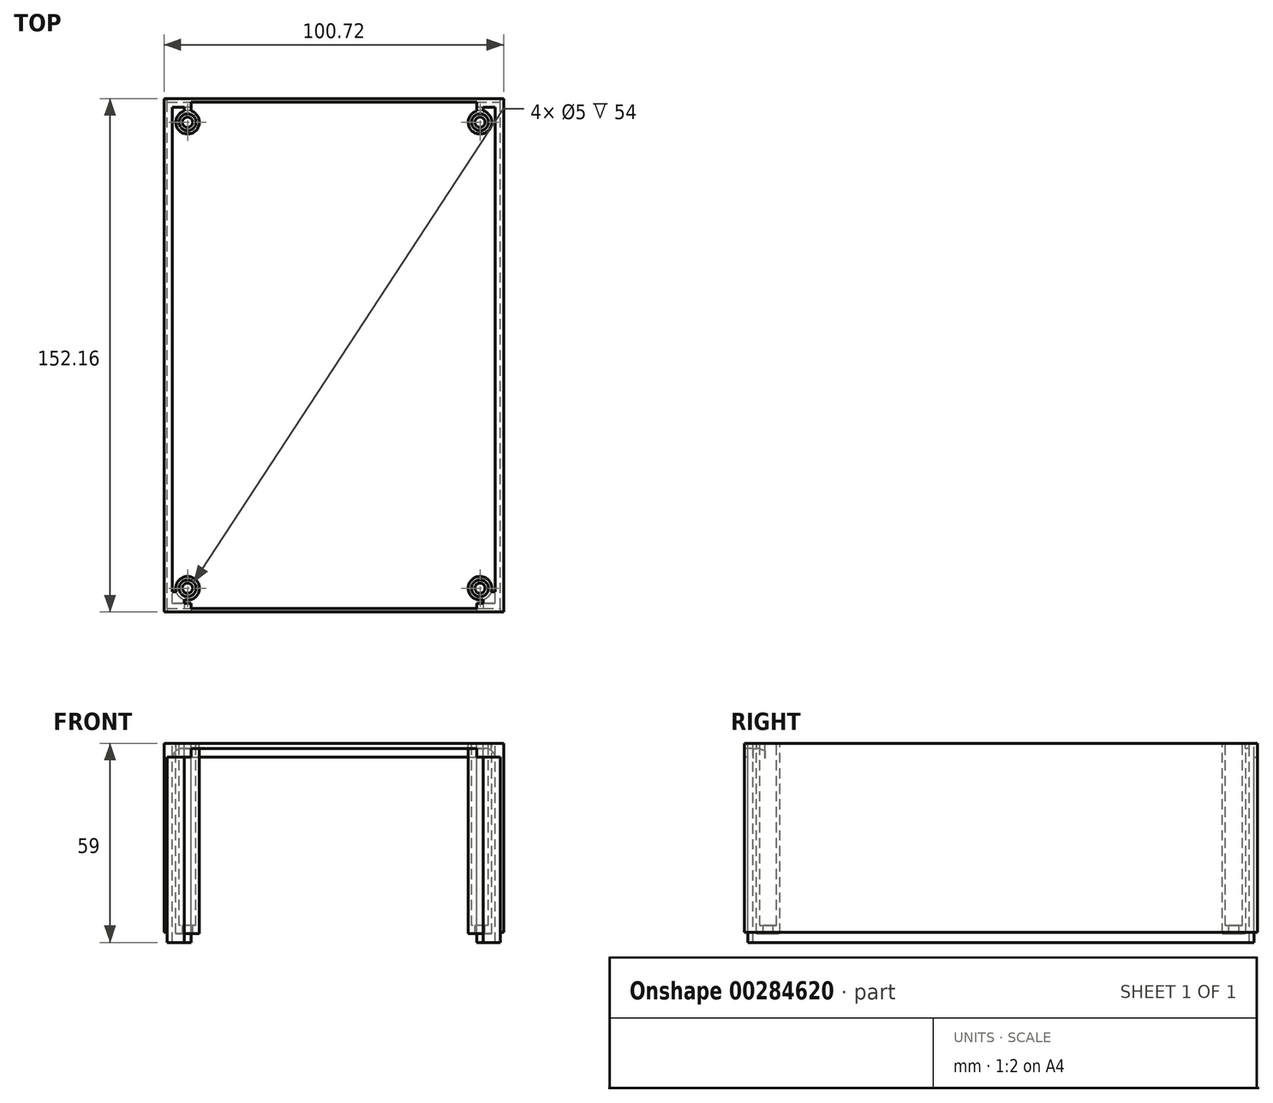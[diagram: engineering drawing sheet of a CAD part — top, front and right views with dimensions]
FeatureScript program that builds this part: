
annotation { "Feature Type Name" : "Feature", "Feature Type Description" : "" }
export const myFeature = defineFeature(function(context is Context, id is Id, definition is map)
    precondition{}
    {
        {
            var Q0;
            Q0=qCreatedBy(makeId("Top.planeOp"),FACE);
            var sketch = newSketch(context, id + "F0", { "sketchPlane" : qUnion([Q0])});
            skLineSegment(sketch, "E0.bottom", {"start": v(50.36, -76.08) * mm, "end": v(-50.36, -76.08) * mm});
            skLineSegment(sketch, "E0.top", {"start": v(50.36, 76.07) * mm, "end": v(-50.36, 76.07) * mm});
            skLineSegment(sketch, "E0.left", {"start": v(50.36, -76.08) * mm, "end": v(50.36, 76.08) * mm});
            skLineSegment(sketch, "E0.right", {"start": v(-50.36, -76.08) * mm, "end": v(-50.36, 76.07) * mm});
            skLineSegment(sketch, "E1.bottom", {"start": v(47.86, -73.58) * mm, "end": v(-47.86, -73.58) * mm});
            skLineSegment(sketch, "E1.top", {"start": v(47.86, 73.58) * mm, "end": v(-47.86, 73.58) * mm});
            skLineSegment(sketch, "E1.left", {"start": v(47.86, -73.58) * mm, "end": v(47.86, 73.58) * mm});
            skLineSegment(sketch, "E1.right", {"start": v(-47.86, -73.58) * mm, "end": v(-47.86, 73.58) * mm});
            skLineSegment(sketch, "E2.bottom", {"start": v(-49.36, -75.08) * mm, "end": v(49.36, -75.08) * mm});
            skLineSegment(sketch, "E2.top", {"start": v(-49.36, 75.08) * mm, "end": v(49.36, 75.08) * mm});
            skLineSegment(sketch, "E2.left", {"start": v(-49.36, -75.08) * mm, "end": v(-49.36, 75.08) * mm});
            skLineSegment(sketch, "E2.right", {"start": v(49.36, -75.08) * mm, "end": v(49.36, 75.08) * mm});
            skPoint(sketch, "E3", {"position": v(0, -76.08) * mm});
            skLineSegment(sketch, "E4", {"start": v(10.09, -76.08) * mm, "end": v(-10.09, -76.08) * mm});
            skLineSegment(sketch, "E5", {"start": v(-10.09, -73.58) * mm, "end": v(10.09, -73.58) * mm});
            skCircle(sketch, "E6", {"center": v(43.36, -69.08) * mm, "radius": 3.5 * mm});
            skCircle(sketch, "E7", {"center": v(43.36, -69.08) * mm, "radius": 2.5 * mm});
            skCircle(sketch, "E8", {"center": v(43.36, -69.08) * mm, "radius": 1.5 * mm});
            skCircle(sketch, "E9", {"center": v(43.36, 69.08) * mm, "radius": 1.5 * mm});
            skCircle(sketch, "E10", {"center": v(43.36, 69.08) * mm, "radius": 2.5 * mm});
            skCircle(sketch, "E11", {"center": v(43.36, 69.08) * mm, "radius": 3.5 * mm});
            skCircle(sketch, "E12", {"center": v(-43.36, 69.08) * mm, "radius": 1.5 * mm});
            skCircle(sketch, "E13", {"center": v(-43.36, 69.08) * mm, "radius": 2.5 * mm});
            skCircle(sketch, "E14", {"center": v(-43.36, 69.08) * mm, "radius": 3.5 * mm});
            skCircle(sketch, "E15", {"center": v(-43.36, -69.08) * mm, "radius": 1.5 * mm});
            skCircle(sketch, "E16", {"center": v(-43.36, -69.08) * mm, "radius": 2.5 * mm});
            skCircle(sketch, "E17", {"center": v(-43.36, -69.08) * mm, "radius": 3.5 * mm});
            skLineSegment(sketch, "E18", {"start": v(49.36, -75.08) * mm, "end": v(49.36, -76.08) * mm});
            skLineSegment(sketch, "E19", {"start": v(-49.36, -75.08) * mm, "end": v(-49.36, -76.08) * mm});
            skLineSegment(sketch, "E20", {"start": v(-49.36, 75.08) * mm, "end": v(-49.36, 76.07) * mm});
            skLineSegment(sketch, "E21", {"start": v(49.36, 75.08) * mm, "end": v(49.36, 76.07) * mm});
            skLineSegment(sketch, "E22", {"start": v(-47.86, -73.58) * mm, "end": v(-49.36, -73.58) * mm});
            skLineSegment(sketch, "E23", {"start": v(47.86, -73.58) * mm, "end": v(49.36, -73.58) * mm});
            skLineSegment(sketch, "E24", {"start": v(47.86, 73.58) * mm, "end": v(49.36, 73.58) * mm});
            skLineSegment(sketch, "E25", {"start": v(-47.86, 73.58) * mm, "end": v(-49.36, 73.58) * mm});
            skLineSegment(sketch, "E26.bottom", {"start": v(47.86, 68.08) * mm, "end": v(45.65, 68.08) * mm});
            skLineSegment(sketch, "E26.top", {"start": v(47.86, 70.08) * mm, "end": v(45.65, 70.08) * mm});
            skLineSegment(sketch, "E26.left", {"start": v(47.86, 68.08) * mm, "end": v(47.86, 70.08) * mm});
            skLineSegment(sketch, "E27.bottom", {"start": v(42.36, 73.58) * mm, "end": v(44.36, 73.58) * mm});
            skLineSegment(sketch, "E27.left", {"start": v(42.36, 73.58) * mm, "end": v(42.36, 71.37) * mm});
            skLineSegment(sketch, "E27.right", {"start": v(44.36, 73.58) * mm, "end": v(44.36, 71.37) * mm});
            skLineSegment(sketch, "E28.bottom", {"start": v(-44.36, 73.58) * mm, "end": v(-42.36, 73.58) * mm});
            skLineSegment(sketch, "E28.left", {"start": v(-44.36, 73.58) * mm, "end": v(-44.36, 71.37) * mm});
            skLineSegment(sketch, "E28.right", {"start": v(-42.36, 73.58) * mm, "end": v(-42.36, 71.37) * mm});
            skLineSegment(sketch, "E29.bottom", {"start": v(-47.86, 70.08) * mm, "end": v(-45.65, 70.08) * mm});
            skLineSegment(sketch, "E29.top", {"start": v(-47.86, 68.08) * mm, "end": v(-45.65, 68.08) * mm});
            skLineSegment(sketch, "E29.left", {"start": v(-47.86, 70.08) * mm, "end": v(-47.86, 68.08) * mm});
            skLineSegment(sketch, "E30.bottom", {"start": v(-47.86, -68.08) * mm, "end": v(-45.65, -68.08) * mm});
            skLineSegment(sketch, "E30.top", {"start": v(-47.86, -70.08) * mm, "end": v(-45.65, -70.08) * mm});
            skLineSegment(sketch, "E30.left", {"start": v(-47.86, -68.08) * mm, "end": v(-47.86, -70.08) * mm});
            skLineSegment(sketch, "E31.bottom", {"start": v(-42.36, -73.58) * mm, "end": v(-44.36, -73.58) * mm});
            skLineSegment(sketch, "E31.left", {"start": v(-42.36, -73.58) * mm, "end": v(-42.36, -71.37) * mm});
            skLineSegment(sketch, "E31.right", {"start": v(-44.36, -73.58) * mm, "end": v(-44.36, -71.37) * mm});
            skLineSegment(sketch, "E32.bottom", {"start": v(44.36, -73.58) * mm, "end": v(42.36, -73.58) * mm});
            skLineSegment(sketch, "E32.left", {"start": v(44.36, -73.58) * mm, "end": v(44.36, -71.37) * mm});
            skLineSegment(sketch, "E32.right", {"start": v(42.36, -73.58) * mm, "end": v(42.36, -71.37) * mm});
            skLineSegment(sketch, "E33.bottom", {"start": v(47.86, -70.08) * mm, "end": v(45.65, -70.08) * mm});
            skLineSegment(sketch, "E33.top", {"start": v(47.86, -68.08) * mm, "end": v(45.65, -68.08) * mm});
            skLineSegment(sketch, "E33.left", {"start": v(47.86, -70.08) * mm, "end": v(47.86, -68.08) * mm});
            skLineSegment(sketch, "E34", {"start": v(-42.36, 73.58) * mm, "end": v(-42.36, 76.07) * mm});
            skLineSegment(sketch, "E35", {"start": v(42.36, 73.58) * mm, "end": v(42.36, 76.07) * mm});
            skLineSegment(sketch, "E36", {"start": v(42.36, -73.58) * mm, "end": v(42.36, -76.08) * mm});
            skLineSegment(sketch, "E37", {"start": v(44.36, -73.58) * mm, "end": v(44.36, -76.08) * mm});
            skLineSegment(sketch, "E38", {"start": v(-44.36, -73.58) * mm, "end": v(-44.36, -76.08) * mm});
            skLineSegment(sketch, "E39", {"start": v(-42.36, -73.58) * mm, "end": v(-42.36, -76.08) * mm});
            skSolve(sketch);
        }
        {
            var Q0;
            Q0 = qSketchRegion(id + "F0", true);
            var Q1;
            Q1=makeQuery(id+"F0.imprint","IMPRINT",FACE,{"disambiguationData":[TD([[makeQuery(id+"F0.imprint","IMPRINT",EDGE,{"derivedFrom":sQuery(id+"F0.wireOp",EDGE,"E1.top")}),1.0]])]});
            var Q2;
            Q2=makeQuery(id+"F0.imprint","IMPRINT",FACE,{"disambiguationData":[TD([[makeQuery(id+"F0.imprint","IMPRINT",EDGE,{"derivedFrom":sQuery(id+"F0.wireOp",EDGE,"E1.top")}),-1.0]])]});
            var Q3;
            {var subQ1=sQuery(id+"F0.wireOp",EDGE,"E2.bottom");Q3=makeQuery(id+"F0.imprint","IMPRINT",FACE,{"disambiguationData":[TD([[makeQuery(id+"F0.imprint","IMPRINT",EDGE,{"derivedFrom":subQ1}),1.0]])]});}
            var Q4;
            {var subQ10=sQuery(id+"F0.wireOp",EDGE,"E5");Q4=makeQuery(id+"F0.imprint","IMPRINT",FACE,{"disambiguationData":[TD([[makeQuery(id+"F0.imprint","IMPRINT",EDGE,{"derivedFrom":subQ10}),1.0]])]});}
            var Q5;
            {var subQ0=sQuery(id+"F0.wireOp",EDGE,"E32.left");var subQ3=sQuery(id+"F0.wireOp",EDGE,"E6");var subQ4=makeQuery(id+"F0.imprint","INTERSECT",VERTEX,{"derivedFrom":[subQ3,subQ0]});Q5=makeQuery(id+"F0.imprint","IMPRINT",FACE,{"disambiguationData":[TD([[makeQuery(id+"F0.imprint","IMPRINT",EDGE,{"disambiguationData":[TD([[subQ4,-1.0]])],"derivedFrom":subQ3}),-1.0]])]});}
            var Q6;
            {var subQ3=sQuery(id+"F0.wireOp",EDGE,"E17");var subQ5=sQuery(id+"F0.wireOp",EDGE,"E31.right");var subQ6=makeQuery(id+"F0.imprint","INTERSECT",VERTEX,{"derivedFrom":[subQ3,subQ5]});Q6=makeQuery(id+"F0.imprint","IMPRINT",FACE,{"disambiguationData":[TD([[makeQuery(id+"F0.imprint","IMPRINT",EDGE,{"disambiguationData":[TD([[subQ6,1.0]])],"derivedFrom":subQ3}),-1.0]])]});}
            var Q7;
            {var subQ0=sQuery(id+"F0.wireOp",EDGE,"E25");Q7=makeQuery(id+"F0.imprint","IMPRINT",FACE,{"disambiguationData":[TD([[makeQuery(id+"F0.imprint","IMPRINT",EDGE,{"derivedFrom":subQ0}),-1.0]])]});}
            var Q8;
            {var subQ0=sQuery(id+"F0.wireOp",EDGE,"E24");Q8=makeQuery(id+"F0.imprint","IMPRINT",FACE,{"disambiguationData":[TD([[makeQuery(id+"F0.imprint","IMPRINT",EDGE,{"derivedFrom":subQ0}),1.0]])]});}
            var Q9;
            {var subQ3=sQuery(id+"F0.wireOp",EDGE,"E23");Q9=makeQuery(id+"F0.imprint","IMPRINT",FACE,{"disambiguationData":[TD([[makeQuery(id+"F0.imprint","IMPRINT",EDGE,{"derivedFrom":subQ3}),-1.0]])]});}
            var Q10;
            {var subQ0=sQuery(id+"F0.wireOp",EDGE,"E22");Q10=makeQuery(id+"F0.imprint","IMPRINT",FACE,{"disambiguationData":[TD([[makeQuery(id+"F0.imprint","IMPRINT",EDGE,{"derivedFrom":subQ0}),1.0]])]});}
            var Q11;
            {var subQ0=sQuery(id+"F0.wireOp",EDGE,"E22");Q11=makeQuery(id+"F0.imprint","IMPRINT",FACE,{"disambiguationData":[TD([[makeQuery(id+"F0.imprint","IMPRINT",EDGE,{"derivedFrom":subQ0}),-1.0]])]});}
            var Q12;
            {var subQ0=sQuery(id+"F0.wireOp",EDGE,"E5");Q12=makeQuery(id+"F0.imprint","IMPRINT",FACE,{"disambiguationData":[TD([[makeQuery(id+"F0.imprint","IMPRINT",EDGE,{"derivedFrom":subQ0}),-1.0]])]});}
            var Q13;
            {var subQ0=sQuery(id+"F0.wireOp",EDGE,"E23");Q13=makeQuery(id+"F0.imprint","IMPRINT",FACE,{"disambiguationData":[TD([[makeQuery(id+"F0.imprint","IMPRINT",EDGE,{"derivedFrom":subQ0}),1.0]])]});}
            extrude(context, id + "F1", {"entities" : qUnion([Q0, Q1, Q2, Q3, Q4, Q5, Q6, Q7, Q8, Q9, Q10, Q11, Q12, Q13]), "oppositeDirection" : true, "depth" : 1.5 * mm});
        }
        {
            var Q0;
            {var subQ0=sQuery(id+"F0.wireOp",EDGE,"E0.right");Q0=makeQuery(id+"F0.imprint","IMPRINT",FACE,{"disambiguationData":[TD([[makeQuery(id+"F0.imprint","IMPRINT",EDGE,{"derivedFrom":subQ0}),-1.0]])]});}
            var Q1;
            {var subQ0=sQuery(id+"F0.wireOp",EDGE,"E0.left");Q1=makeQuery(id+"F0.imprint","IMPRINT",FACE,{"disambiguationData":[TD([[makeQuery(id+"F0.imprint","IMPRINT",EDGE,{"derivedFrom":subQ0}),1.0]])]});}
            extrude(context, id + "F2", {"entities" : qUnion([Q0, Q1]), "operationType" : NewBodyOperationType.ADD, "oppositeDirection" : true, "depth" : 56 * mm});
        }
        {
            var Q0;
            Q0=makeQuery(id+"F0.imprint","IMPRINT",FACE,{"disambiguationData":[TD([[makeQuery(id+"F0.imprint","IMPRINT",EDGE,{"derivedFrom":sQuery(id+"F0.wireOp",EDGE,"E1.right")}),1.0]])]});
            var Q1;
            Q1=makeQuery(id+"F0.imprint","IMPRINT",FACE,{"disambiguationData":[TD([[makeQuery(id+"F0.imprint","IMPRINT",EDGE,{"derivedFrom":sQuery(id+"F0.wireOp",EDGE,"E1.left")}),-1.0]])]});
            var Q2;
            {var subQ0=sQuery(id+"F0.wireOp",EDGE,"E22");Q2=makeQuery(id+"F0.imprint","IMPRINT",FACE,{"disambiguationData":[TD([[makeQuery(id+"F0.imprint","IMPRINT",EDGE,{"derivedFrom":subQ0}),1.0]])]});}
            var Q3;
            {var subQ5=sQuery(id+"F0.wireOp",EDGE,"E31.bottom");Q3=makeQuery(id+"F0.imprint","IMPRINT",FACE,{"disambiguationData":[TD([[makeQuery(id+"F0.imprint","IMPRINT",EDGE,{"derivedFrom":subQ5}),1.0]])]});}
            var Q4;
            {var subQ5=sQuery(id+"F0.wireOp",EDGE,"E32.bottom");Q4=makeQuery(id+"F0.imprint","IMPRINT",FACE,{"disambiguationData":[TD([[makeQuery(id+"F0.imprint","IMPRINT",EDGE,{"derivedFrom":subQ5}),1.0]])]});}
            var Q5;
            {var subQ3=sQuery(id+"F0.wireOp",EDGE,"E23");Q5=makeQuery(id+"F0.imprint","IMPRINT",FACE,{"disambiguationData":[TD([[makeQuery(id+"F0.imprint","IMPRINT",EDGE,{"derivedFrom":subQ3}),-1.0]])]});}
            var Q6;
            {var subQ0=sQuery(id+"F0.wireOp",EDGE,"E24");Q6=makeQuery(id+"F0.imprint","IMPRINT",FACE,{"disambiguationData":[TD([[makeQuery(id+"F0.imprint","IMPRINT",EDGE,{"derivedFrom":subQ0}),1.0]])]});}
            var Q7;
            {var subQ0=sQuery(id+"F0.wireOp",EDGE,"E25");Q7=makeQuery(id+"F0.imprint","IMPRINT",FACE,{"disambiguationData":[TD([[makeQuery(id+"F0.imprint","IMPRINT",EDGE,{"derivedFrom":subQ0}),-1.0]])]});}
            extrude(context, id + "F3", {"entities" : qUnion([Q0, Q1, Q2, Q3, Q4, Q5, Q6, Q7]), "operationType" : NewBodyOperationType.ADD, "oppositeDirection" : true, "depth" : 59 * mm});
        }
        {
            var Q0;
            Q0=makeQuery(id+"F0.imprint","IMPRINT",FACE,{"disambiguationData":[TD([[makeQuery(id+"F0.imprint","IMPRINT",EDGE,{"derivedFrom":sQuery(id+"F0.wireOp",EDGE,"E2.bottom")}),-1.0]])]});
            var Q1;
            Q1=makeQuery(id+"F0.imprint","IMPRINT",FACE,{"disambiguationData":[TD([[makeQuery(id+"F0.imprint","IMPRINT",EDGE,{"derivedFrom":sQuery(id+"F0.wireOp",EDGE,"E2.top")}),1.0]])]});
            extrude(context, id + "F4", {"entities" : qUnion([Q0, Q1]), "operationType" : NewBodyOperationType.ADD, "oppositeDirection" : true, "depth" : 4 * mm});
        }
        {
            var Q0;
            {var subQ5=sQuery(id+"F0.wireOp",EDGE,"E32.bottom");Q0=makeQuery(id+"F0.imprint","IMPRINT",FACE,{"disambiguationData":[TD([[makeQuery(id+"F0.imprint","IMPRINT",EDGE,{"derivedFrom":subQ5}),-1.0]])]});}
            var Q1;
            {var subQ0=sQuery(id+"F0.wireOp",EDGE,"E32.left");var subQ1=sQuery(id+"F0.wireOp",EDGE,"E6");var subQ2=makeQuery(id+"F0.imprint","INTERSECT",VERTEX,{"derivedFrom":[subQ1,subQ0]});Q1=makeQuery(id+"F0.imprint","IMPRINT",FACE,{"disambiguationData":[TD([[makeQuery(id+"F0.imprint","IMPRINT",EDGE,{"disambiguationData":[TD([[subQ2,1.0]])],"derivedFrom":subQ1}),1.0]])]});}
            var Q2;
            {var subQ0=sQuery(id+"F0.wireOp",EDGE,"E32.right");var subQ1=sQuery(id+"F0.wireOp",EDGE,"E6");var subQ2=makeQuery(id+"F0.imprint","INTERSECT",VERTEX,{"derivedFrom":[subQ1,subQ0]});Q2=makeQuery(id+"F0.imprint","IMPRINT",FACE,{"disambiguationData":[TD([[makeQuery(id+"F0.imprint","IMPRINT",EDGE,{"disambiguationData":[TD([[subQ2,1.0]])],"derivedFrom":subQ1}),1.0]])]});}
            var Q3;
            Q3=makeQuery(id+"F0.imprint","IMPRINT",FACE,{"disambiguationData":[TD([[makeQuery(id+"F0.imprint","IMPRINT",EDGE,{"derivedFrom":sQuery(id+"F0.wireOp",EDGE,"E8")}),-1.0]])]});
            var Q4;
            {var subQ5=sQuery(id+"F0.wireOp",EDGE,"E33.left");Q4=makeQuery(id+"F0.imprint","IMPRINT",FACE,{"disambiguationData":[TD([[makeQuery(id+"F0.imprint","IMPRINT",EDGE,{"derivedFrom":subQ5}),1.0]])]});}
            var Q5;
            {var subQ0=sQuery(id+"F0.wireOp",EDGE,"E33.bottom");var subQ1=sQuery(id+"F0.wireOp",EDGE,"E6");var subQ2=makeQuery(id+"F0.imprint","INTERSECT",VERTEX,{"derivedFrom":[subQ1,subQ0]});Q5=makeQuery(id+"F0.imprint","IMPRINT",FACE,{"disambiguationData":[TD([[makeQuery(id+"F0.imprint","IMPRINT",EDGE,{"disambiguationData":[TD([[subQ2,-1.0]])],"derivedFrom":subQ1}),1.0]])]});}
            var Q6;
            {var subQ0=sQuery(id+"F0.wireOp",EDGE,"E32.left");var subQ1=sQuery(id+"F0.wireOp",EDGE,"E6");var subQ2=makeQuery(id+"F0.imprint","INTERSECT",VERTEX,{"derivedFrom":[subQ1,subQ0]});Q6=makeQuery(id+"F0.imprint","IMPRINT",FACE,{"disambiguationData":[TD([[makeQuery(id+"F0.imprint","IMPRINT",EDGE,{"disambiguationData":[TD([[subQ2,-1.0]])],"derivedFrom":subQ1}),1.0]])]});}
            var Q7;
            {var subQ5=sQuery(id+"F0.wireOp",EDGE,"E31.bottom");Q7=makeQuery(id+"F0.imprint","IMPRINT",FACE,{"disambiguationData":[TD([[makeQuery(id+"F0.imprint","IMPRINT",EDGE,{"derivedFrom":subQ5}),-1.0]])]});}
            var Q8;
            {var subQ0=sQuery(id+"F0.wireOp",EDGE,"E31.left");var subQ1=sQuery(id+"F0.wireOp",EDGE,"E16");var subQ2=makeQuery(id+"F0.imprint","INTERSECT",VERTEX,{"derivedFrom":[subQ1,subQ0]});Q8=makeQuery(id+"F0.imprint","IMPRINT",FACE,{"disambiguationData":[TD([[makeQuery(id+"F0.imprint","IMPRINT",EDGE,{"disambiguationData":[TD([[subQ2,1.0]])],"derivedFrom":subQ1}),-1.0]])]});}
            var Q9;
            {var subQ0=sQuery(id+"F0.wireOp",EDGE,"E30.bottom");var subQ1=sQuery(id+"F0.wireOp",EDGE,"E16");var subQ2=makeQuery(id+"F0.imprint","INTERSECT",VERTEX,{"derivedFrom":[subQ1,subQ0]});Q9=makeQuery(id+"F0.imprint","IMPRINT",FACE,{"disambiguationData":[TD([[makeQuery(id+"F0.imprint","IMPRINT",EDGE,{"disambiguationData":[TD([[subQ2,1.0]])],"derivedFrom":subQ1}),-1.0]])]});}
            var Q10;
            Q10=makeQuery(id+"F0.imprint","IMPRINT",FACE,{"disambiguationData":[TD([[makeQuery(id+"F0.imprint","IMPRINT",EDGE,{"derivedFrom":sQuery(id+"F0.wireOp",EDGE,"E15")}),-1.0]])]});
            var Q11;
            {var subQ0=sQuery(id+"F0.wireOp",EDGE,"E30.top");var subQ1=sQuery(id+"F0.wireOp",EDGE,"E16");var subQ2=makeQuery(id+"F0.imprint","INTERSECT",VERTEX,{"derivedFrom":[subQ1,subQ0]});Q11=makeQuery(id+"F0.imprint","IMPRINT",FACE,{"disambiguationData":[TD([[makeQuery(id+"F0.imprint","IMPRINT",EDGE,{"disambiguationData":[TD([[subQ2,-1.0]])],"derivedFrom":subQ1}),-1.0]])]});}
            var Q12;
            {var subQ5=sQuery(id+"F0.wireOp",EDGE,"E30.left");Q12=makeQuery(id+"F0.imprint","IMPRINT",FACE,{"disambiguationData":[TD([[makeQuery(id+"F0.imprint","IMPRINT",EDGE,{"derivedFrom":subQ5}),1.0]])]});}
            var Q13;
            {var subQ0=sQuery(id+"F0.wireOp",EDGE,"E30.bottom");var subQ1=sQuery(id+"F0.wireOp",EDGE,"E16");var subQ2=makeQuery(id+"F0.imprint","INTERSECT",VERTEX,{"derivedFrom":[subQ1,subQ0]});Q13=makeQuery(id+"F0.imprint","IMPRINT",FACE,{"disambiguationData":[TD([[makeQuery(id+"F0.imprint","IMPRINT",EDGE,{"disambiguationData":[TD([[subQ2,-1.0]])],"derivedFrom":subQ1}),-1.0]])]});}
            var Q14;
            {var subQ5=sQuery(id+"F0.wireOp",EDGE,"E26.left");Q14=makeQuery(id+"F0.imprint","IMPRINT",FACE,{"disambiguationData":[TD([[makeQuery(id+"F0.imprint","IMPRINT",EDGE,{"derivedFrom":subQ5}),1.0]])]});}
            var Q15;
            {var subQ0=sQuery(id+"F0.wireOp",EDGE,"E26.bottom");var subQ1=sQuery(id+"F0.wireOp",EDGE,"E10");var subQ2=makeQuery(id+"F0.imprint","INTERSECT",VERTEX,{"derivedFrom":[subQ1,subQ0]});Q15=makeQuery(id+"F0.imprint","IMPRINT",FACE,{"disambiguationData":[TD([[makeQuery(id+"F0.imprint","IMPRINT",EDGE,{"disambiguationData":[TD([[subQ2,-1.0]])],"derivedFrom":subQ1}),-1.0]])]});}
            var Q16;
            {var subQ0=sQuery(id+"F0.wireOp",EDGE,"E26.bottom");var subQ1=sQuery(id+"F0.wireOp",EDGE,"E10");var subQ2=makeQuery(id+"F0.imprint","INTERSECT",VERTEX,{"derivedFrom":[subQ1,subQ0]});Q16=makeQuery(id+"F0.imprint","IMPRINT",FACE,{"disambiguationData":[TD([[makeQuery(id+"F0.imprint","IMPRINT",EDGE,{"disambiguationData":[TD([[subQ2,1.0]])],"derivedFrom":subQ1}),-1.0]])]});}
            var Q17;
            {var subQ0=sQuery(id+"F0.wireOp",EDGE,"E26.top");var subQ1=sQuery(id+"F0.wireOp",EDGE,"E10");var subQ2=makeQuery(id+"F0.imprint","INTERSECT",VERTEX,{"derivedFrom":[subQ1,subQ0]});Q17=makeQuery(id+"F0.imprint","IMPRINT",FACE,{"disambiguationData":[TD([[makeQuery(id+"F0.imprint","IMPRINT",EDGE,{"disambiguationData":[TD([[subQ2,-1.0]])],"derivedFrom":subQ1}),-1.0]])]});}
            var Q18;
            {var subQ0=sQuery(id+"F0.wireOp",EDGE,"E27.left");var subQ1=sQuery(id+"F0.wireOp",EDGE,"E10");var subQ2=makeQuery(id+"F0.imprint","INTERSECT",VERTEX,{"derivedFrom":[subQ1,subQ0]});Q18=makeQuery(id+"F0.imprint","IMPRINT",FACE,{"disambiguationData":[TD([[makeQuery(id+"F0.imprint","IMPRINT",EDGE,{"disambiguationData":[TD([[subQ2,1.0]])],"derivedFrom":subQ1}),-1.0]])]});}
            var Q19;
            {var subQ5=sQuery(id+"F0.wireOp",EDGE,"E27.bottom");Q19=makeQuery(id+"F0.imprint","IMPRINT",FACE,{"disambiguationData":[TD([[makeQuery(id+"F0.imprint","IMPRINT",EDGE,{"derivedFrom":subQ5}),-1.0]])]});}
            var Q20;
            Q20=makeQuery(id+"F0.imprint","IMPRINT",FACE,{"disambiguationData":[TD([[makeQuery(id+"F0.imprint","IMPRINT",EDGE,{"derivedFrom":sQuery(id+"F0.wireOp",EDGE,"E9")}),-1.0]])]});
            var Q21;
            {var subQ5=sQuery(id+"F0.wireOp",EDGE,"E28.bottom");Q21=makeQuery(id+"F0.imprint","IMPRINT",FACE,{"disambiguationData":[TD([[makeQuery(id+"F0.imprint","IMPRINT",EDGE,{"derivedFrom":subQ5}),-1.0]])]});}
            var Q22;
            {var subQ0=sQuery(id+"F0.wireOp",EDGE,"E28.left");var subQ1=sQuery(id+"F0.wireOp",EDGE,"E13");var subQ2=makeQuery(id+"F0.imprint","INTERSECT",VERTEX,{"derivedFrom":[subQ1,subQ0]});Q22=makeQuery(id+"F0.imprint","IMPRINT",FACE,{"disambiguationData":[TD([[makeQuery(id+"F0.imprint","IMPRINT",EDGE,{"disambiguationData":[TD([[subQ2,1.0]])],"derivedFrom":subQ1}),-1.0]])]});}
            var Q23;
            {var subQ0=sQuery(id+"F0.wireOp",EDGE,"E28.left");var subQ1=sQuery(id+"F0.wireOp",EDGE,"E13");var subQ2=makeQuery(id+"F0.imprint","INTERSECT",VERTEX,{"derivedFrom":[subQ1,subQ0]});Q23=makeQuery(id+"F0.imprint","IMPRINT",FACE,{"disambiguationData":[TD([[makeQuery(id+"F0.imprint","IMPRINT",EDGE,{"disambiguationData":[TD([[subQ2,-1.0]])],"derivedFrom":subQ1}),-1.0]])]});}
            var Q24;
            {var subQ0=sQuery(id+"F0.wireOp",EDGE,"E29.bottom");var subQ1=sQuery(id+"F0.wireOp",EDGE,"E13");var subQ2=makeQuery(id+"F0.imprint","INTERSECT",VERTEX,{"derivedFrom":[subQ1,subQ0]});Q24=makeQuery(id+"F0.imprint","IMPRINT",FACE,{"disambiguationData":[TD([[makeQuery(id+"F0.imprint","IMPRINT",EDGE,{"disambiguationData":[TD([[subQ2,-1.0]])],"derivedFrom":subQ1}),-1.0]])]});}
            var Q25;
            {var subQ5=sQuery(id+"F0.wireOp",EDGE,"E29.left");Q25=makeQuery(id+"F0.imprint","IMPRINT",FACE,{"disambiguationData":[TD([[makeQuery(id+"F0.imprint","IMPRINT",EDGE,{"derivedFrom":subQ5}),1.0]])]});}
            var Q26;
            Q26=makeQuery(id+"F0.imprint","IMPRINT",FACE,{"disambiguationData":[TD([[makeQuery(id+"F0.imprint","IMPRINT",EDGE,{"derivedFrom":sQuery(id+"F0.wireOp",EDGE,"E12")}),-1.0]])]});
            var Q27;
            {var subQ0=sQuery(id+"F0.wireOp",EDGE,"E28.right");var subQ1=sQuery(id+"F0.wireOp",EDGE,"E13");var subQ2=makeQuery(id+"F0.imprint","INTERSECT",VERTEX,{"derivedFrom":[subQ1,subQ0]});Q27=makeQuery(id+"F0.imprint","IMPRINT",FACE,{"disambiguationData":[TD([[makeQuery(id+"F0.imprint","IMPRINT",EDGE,{"disambiguationData":[TD([[subQ2,1.0]])],"derivedFrom":subQ1}),-1.0]])]});}
            extrude(context, id + "F5", {"entities" : qUnion([Q0, Q1, Q2, Q3, Q4, Q5, Q6, Q7, Q8, Q9, Q10, Q11, Q12, Q13, Q14, Q15, Q16, Q17, Q18, Q19, Q20, Q21, Q22, Q23, Q24, Q25, Q26, Q27]), "operationType" : NewBodyOperationType.ADD, "oppositeDirection" : true, "depth" : 56.36 * mm});
        }
        {
            var Q0;
            Q0=makeQuery(id+"F0.imprint","IMPRINT",FACE,{"disambiguationData":[TD([[makeQuery(id+"F0.imprint","IMPRINT",EDGE,{"derivedFrom":sQuery(id+"F0.wireOp",EDGE,"E12")}),-1.0]])]});
            var Q1;
            Q1=makeQuery(id+"F0.imprint","IMPRINT",FACE,{"disambiguationData":[TD([[makeQuery(id+"F0.imprint","IMPRINT",EDGE,{"derivedFrom":sQuery(id+"F0.wireOp",EDGE,"E9")}),-1.0]])]});
            var Q2;
            Q2=makeQuery(id+"F0.imprint","IMPRINT",FACE,{"disambiguationData":[TD([[makeQuery(id+"F0.imprint","IMPRINT",EDGE,{"derivedFrom":sQuery(id+"F0.wireOp",EDGE,"E15")}),-1.0]])]});
            var Q3;
            Q3=makeQuery(id+"F0.imprint","IMPRINT",FACE,{"disambiguationData":[TD([[makeQuery(id+"F0.imprint","IMPRINT",EDGE,{"derivedFrom":sQuery(id+"F0.wireOp",EDGE,"E8")}),-1.0]])]});
            extrude(context, id + "F6", {"entities" : qUnion([Q0, Q1, Q2, Q3]), "operationType" : NewBodyOperationType.REMOVE, "oppositeDirection" : true, "depth" : 54 * mm});
        }
        {
            var Q0;
            {var subQ0=sQuery(id+"F0.wireOp",EDGE,"E33.left");var subQ1=sQuery(id+"F0.wireOp",EDGE,"E26.left");Q0=makeQuery(id+"F3.boolean.opBoolean","INTERSECT",EDGE,{"disambiguationData":[OD(0.0)],"derivedFrom":[makeQuery(id+"F1.opExtrude","CAP_FACE",FACE,{"disambiguationData":[OSD([sQuery(id+"F0.wireOp",EDGE,"E0.bottom"),sQuery(id+"F0.wireOp",EDGE,"E0.top"),sQuery(id+"F0.wireOp",EDGE,"E0.left"),sQuery(id+"F0.wireOp",EDGE,"E0.right"),sQuery(id+"F0.wireOp",EDGE,"E4"),sQuery(id+"F0.wireOp",EDGE,"E6"),sQuery(id+"F0.wireOp",EDGE,"E11"),sQuery(id+"F0.wireOp",EDGE,"E14"),sQuery(id+"F0.wireOp",EDGE,"E17"),sQuery(id+"F0.wireOp",EDGE,"E26.bottom"),sQuery(id+"F0.wireOp",EDGE,"E26.top"),subQ1,sQuery(id+"F0.wireOp",EDGE,"E27.bottom"),sQuery(id+"F0.wireOp",EDGE,"E27.left"),sQuery(id+"F0.wireOp",EDGE,"E27.right"),sQuery(id+"F0.wireOp",EDGE,"E28.bottom"),sQuery(id+"F0.wireOp",EDGE,"E28.left"),sQuery(id+"F0.wireOp",EDGE,"E28.right"),sQuery(id+"F0.wireOp",EDGE,"E29.bottom"),sQuery(id+"F0.wireOp",EDGE,"E29.top"),sQuery(id+"F0.wireOp",EDGE,"E29.left"),sQuery(id+"F0.wireOp",EDGE,"E30.bottom"),sQuery(id+"F0.wireOp",EDGE,"E30.top"),sQuery(id+"F0.wireOp",EDGE,"E30.left"),sQuery(id+"F0.wireOp",EDGE,"E31.bottom"),sQuery(id+"F0.wireOp",EDGE,"E31.left"),sQuery(id+"F0.wireOp",EDGE,"E31.right"),sQuery(id+"F0.wireOp",EDGE,"E32.bottom"),sQuery(id+"F0.wireOp",EDGE,"E32.left"),sQuery(id+"F0.wireOp",EDGE,"E32.right"),sQuery(id+"F0.wireOp",EDGE,"E33.bottom"),sQuery(id+"F0.wireOp",EDGE,"E33.top"),subQ0])],"isStart":false}),makeQuery(id+"F3.opExtrude","SWEPT_FACE",FACE,{"disambiguationData":[OSD([sQuery(id+"F0.wireOp",EDGE,"E1.left"),subQ1,subQ0])]})]});}
            var Q1;
            {var subQ0=sQuery(id+"F0.wireOp",EDGE,"E30.left");var subQ1=sQuery(id+"F0.wireOp",EDGE,"E29.left");Q1=makeQuery(id+"F3.boolean.opBoolean","INTERSECT",EDGE,{"disambiguationData":[OD(0.0)],"derivedFrom":[makeQuery(id+"F1.opExtrude","CAP_FACE",FACE,{"disambiguationData":[OSD([sQuery(id+"F0.wireOp",EDGE,"E0.bottom"),sQuery(id+"F0.wireOp",EDGE,"E0.top"),sQuery(id+"F0.wireOp",EDGE,"E0.left"),sQuery(id+"F0.wireOp",EDGE,"E0.right"),sQuery(id+"F0.wireOp",EDGE,"E4"),sQuery(id+"F0.wireOp",EDGE,"E6"),sQuery(id+"F0.wireOp",EDGE,"E11"),sQuery(id+"F0.wireOp",EDGE,"E14"),sQuery(id+"F0.wireOp",EDGE,"E17"),sQuery(id+"F0.wireOp",EDGE,"E26.bottom"),sQuery(id+"F0.wireOp",EDGE,"E26.top"),sQuery(id+"F0.wireOp",EDGE,"E26.left"),sQuery(id+"F0.wireOp",EDGE,"E27.bottom"),sQuery(id+"F0.wireOp",EDGE,"E27.left"),sQuery(id+"F0.wireOp",EDGE,"E27.right"),sQuery(id+"F0.wireOp",EDGE,"E28.bottom"),sQuery(id+"F0.wireOp",EDGE,"E28.left"),sQuery(id+"F0.wireOp",EDGE,"E28.right"),sQuery(id+"F0.wireOp",EDGE,"E29.bottom"),sQuery(id+"F0.wireOp",EDGE,"E29.top"),subQ1,sQuery(id+"F0.wireOp",EDGE,"E30.bottom"),sQuery(id+"F0.wireOp",EDGE,"E30.top"),subQ0,sQuery(id+"F0.wireOp",EDGE,"E31.bottom"),sQuery(id+"F0.wireOp",EDGE,"E31.left"),sQuery(id+"F0.wireOp",EDGE,"E31.right"),sQuery(id+"F0.wireOp",EDGE,"E32.bottom"),sQuery(id+"F0.wireOp",EDGE,"E32.left"),sQuery(id+"F0.wireOp",EDGE,"E32.right"),sQuery(id+"F0.wireOp",EDGE,"E33.bottom"),sQuery(id+"F0.wireOp",EDGE,"E33.top"),sQuery(id+"F0.wireOp",EDGE,"E33.left")])],"isStart":false}),makeQuery(id+"F3.opExtrude","SWEPT_FACE",FACE,{"disambiguationData":[OSD([sQuery(id+"F0.wireOp",EDGE,"E1.right"),subQ1,subQ0])]})]});}
            fillet(context, id + "F7", {"entities" : qUnion([Q0, Q1]), "radius" : 3 * mm, "tangentPropagation" : true, "allowEdgeOverflow" : false});
        }
    });
